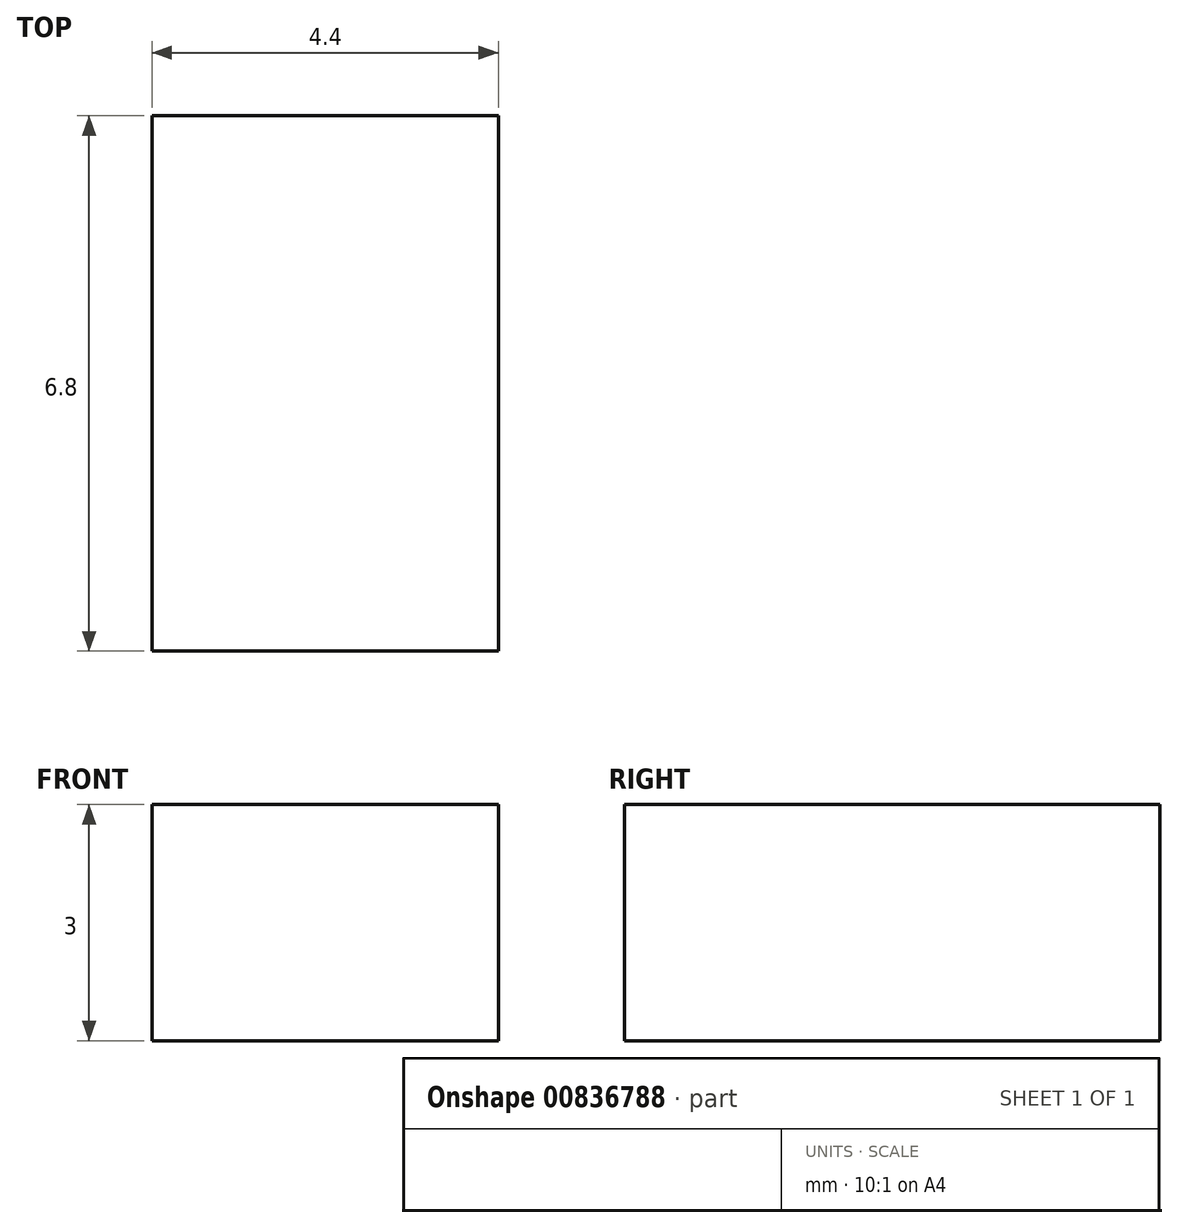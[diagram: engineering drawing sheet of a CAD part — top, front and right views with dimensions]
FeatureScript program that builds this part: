
annotation { "Feature Type Name" : "Feature", "Feature Type Description" : "" }
export const myFeature = defineFeature(function(context is Context, id is Id, definition is map)
    precondition{}
    {
        {
            var Q0;
            Q0=qCreatedBy(makeId("Top.planeOp"),FACE);
            var sketch = newSketch(context, id + "F0", { "sketchPlane" : qUnion([Q0])});
            skLineSegment(sketch, "E0.bottom", {"start": v(2.2, -3.4) * mm, "end": v(-2.2, -3.4) * mm});
            skLineSegment(sketch, "E0.top", {"start": v(2.2, 3.4) * mm, "end": v(-2.2, 3.4) * mm});
            skLineSegment(sketch, "E0.left", {"start": v(2.2, -3.4) * mm, "end": v(2.2, 3.4) * mm});
            skLineSegment(sketch, "E0.right", {"start": v(-2.2, -3.4) * mm, "end": v(-2.2, 3.4) * mm});
            skPoint(sketch, "E0.middle", {"position": v(0, 0) * mm});
            skSolve(sketch);
        }
        {
            var Q0;
            Q0=makeQuery(id+"F0.imprint","IMPRINT",FACE,{"disambiguationData":[TD([[makeQuery(id+"F0.imprint","IMPRINT",EDGE,{"derivedFrom":sQuery(id+"F0.wireOp",EDGE,"E0.bottom")}),-1.0]])]});
            extrude(context, id + "F1", {"entities" : qUnion([Q0]), "depth" : 3 * mm, "offsetDistance" : 25 * mm});
        }
    });
